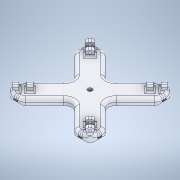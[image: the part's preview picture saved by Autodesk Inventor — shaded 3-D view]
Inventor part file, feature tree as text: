
AUTODESK INVENTOR PART (.ipt)
format: ipt  version: 2022 (Build 260153000, 153)  size: 627,200 bytes
history: native  units: in
note: dims shown in document units (in); Inventor stores cm internally (conversion verified against a paired STEP export)
features: sketch x5, extrude x3, hole x3, fillet x3, chamfer x1, pattern_circular x1
ambient origin geometry x8: Origin, YZ Plane, XZ Plane, XY Plane, X Axis, Y Axis, Z Axis, Center Point
bodies: Solid1 (feature_tree)
feature tree (16):
  extrude  "Extrusion1"  Depth=2.9528in
  hole  "Hole2"  [1 undecoded]
  chamfer  "Chamfer1"  Distance=0.0394in Angle=45.0deg
  hole  "Hole5"  [1 undecoded]
  extrude  "Extrusion5"  Depth=1.4764in
  fillet  "Fillet3"  Radius=0.2165in
  hole  "Hole7"  [1 undecoded]
  pattern_circular  "Circular Pattern6"  [2 undecoded]
  extrude  "Extrusion14"  Depth=0.1969in TaperAngle=0.0deg
  fillet  "Fillet8"  Radius=0.1575in
  fillet  "Fillet9"  Radius=0.1969in
  sketch  "Sketch1"  dims[d0=2.9528in d1=2.9528in]
  sketch  "Sketch4"  dims[d2=0.2165in d3=0.0in]
  sketch  "Sketch9"  dims[d15=0.1575in d16=0.2362in d17=1.0039in d18=0.0591in d19=90.0deg d20=0.315in d21=0.8108in d22=1.4764in]
  sketch  "Sketch13"  dims[d23=1.4764in d24=0.0394in d25=0.0787in d26=45.0deg]
  sketch  "Sketch24"  dims[d82=0.1575in d83=0.2362in d84=0.1575in d85=0.0787in d86=90.0deg d87=0.315in d88=0.8108in d89=1.1024in d90=1.4764in d97=0.2165in d98=0.1575in d99=0.9276in d100=0.1969in d101=0.0in d102=0.1575in d103=0.1969in d105=0.2165in d106=0.1082in d107=0.0591in d117=0.0787in d118=0.2362in d119=0.1575in d120=0.0787in d121=90.0deg d122=0.315in d123=0.8108in d124=0.1083in d125=0.0787in d129=1.5748in d130=360.0deg d199=135.0deg d200=90.0deg d201=0.5315in d202=0.5315in d203=1.1811in d205=180.0deg d207=0.0394in d208=0.0in d209=0.2756in d210=0.1181in d217=1.5748in d219=360.0deg d131=0.0197in d132=0.0344in d155=0.0394in d156=0.0394in d157=0.0394in d158=0.0059in d159=0.0098in d160=0.0148in d161=0.5635in d162=0.0295in d163=0.8108in d164=0.0025in d165=0.0295in d166=0.0148in]
note: 5 required parameter values undecoded (feature->parameter linkage not recoverable at this tier; creation-order binding heuristic only, values carry confidence <= 0.55)
